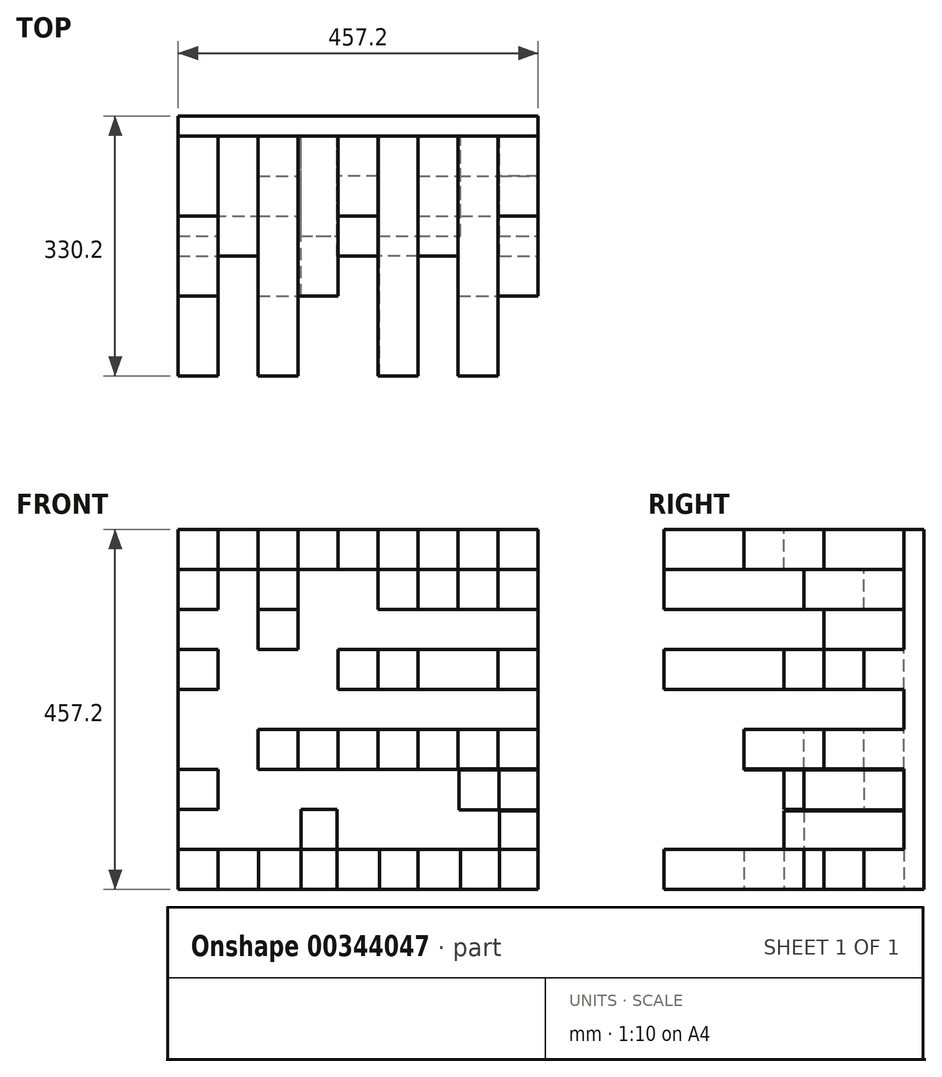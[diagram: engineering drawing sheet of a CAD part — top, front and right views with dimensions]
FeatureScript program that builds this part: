
annotation { "Feature Type Name" : "Feature", "Feature Type Description" : "" }
export const myFeature = defineFeature(function(context is Context, id is Id, definition is map)
    precondition{}
    {
        {
            var Q0;
            Q0=qCreatedBy(makeId("Front.planeOp"),FACE);
            var sketch = newSketch(context, id + "F0", { "sketchPlane" : qUnion([Q0])});
            skLineSegment(sketch, "E0.bottom", {"start": v(-230.78, 329.48) * mm, "end": v(226.42, 329.48) * mm});
            skLineSegment(sketch, "E0.top", {"start": v(-230.78, -127.72) * mm, "end": v(226.42, -127.72) * mm});
            skLineSegment(sketch, "E0.left", {"start": v(-230.78, 329.48) * mm, "end": v(-230.78, -127.72) * mm});
            skLineSegment(sketch, "E0.right", {"start": v(226.42, 329.48) * mm, "end": v(226.42, -127.72) * mm});
            skSolve(sketch);
        }
        {
            var Q0;
            Q0=makeQuery(id+"F0.imprint","IMPRINT",FACE,{"disambiguationData":[TD([[makeQuery(id+"F0.imprint","IMPRINT",EDGE,{"derivedFrom":sQuery(id+"F0.wireOp",EDGE,"E0.bottom")}),-1.0]])]});
            extrude(context, id + "F1", {"entities" : qUnion([Q0]), "depth" : 25.4 * mm});
        }
        {
            var Q0;
            Q0=makeQuery(id+"F1.opExtrude","CAP_FACE",FACE,{"disambiguationData":[OSD([sQuery(id+"F0.wireOp",EDGE,"E0.bottom"),sQuery(id+"F0.wireOp",EDGE,"E0.top"),sQuery(id+"F0.wireOp",EDGE,"E0.left"),sQuery(id+"F0.wireOp",EDGE,"E0.right")])],"isStart":false});
            var sketch = newSketch(context, id + "F2", { "sketchPlane" : qUnion([Q0])});
            skLineSegment(sketch, "E1.bottom", {"start": v(-230.78, 329.48) * mm, "end": v(-179.98, 329.48) * mm});
            skLineSegment(sketch, "E1.top", {"start": v(-230.78, 278.68) * mm, "end": v(-179.98, 278.68) * mm});
            skLineSegment(sketch, "E1.left", {"start": v(-230.78, 329.48) * mm, "end": v(-230.78, 278.68) * mm});
            skLineSegment(sketch, "E1.right", {"start": v(-179.98, 329.48) * mm, "end": v(-179.98, 278.68) * mm});
            skLineSegment(sketch, "E2.bottom", {"start": v(-179.98, 278.68) * mm, "end": v(-129.18, 278.68) * mm});
            skLineSegment(sketch, "E2.top", {"start": v(-179.98, 329.48) * mm, "end": v(-129.18, 329.48) * mm});
            skLineSegment(sketch, "E2.left", {"start": v(-179.98, 278.68) * mm, "end": v(-179.98, 329.48) * mm});
            skLineSegment(sketch, "E2.right", {"start": v(-129.18, 278.68) * mm, "end": v(-129.18, 329.48) * mm});
            skLineSegment(sketch, "E3.bottom", {"start": v(-129.18, 278.68) * mm, "end": v(-78.38, 278.68) * mm});
            skLineSegment(sketch, "E3.top", {"start": v(-129.18, 329.48) * mm, "end": v(-78.38, 329.48) * mm});
            skLineSegment(sketch, "E3.right", {"start": v(-78.38, 278.68) * mm, "end": v(-78.38, 329.48) * mm});
            skLineSegment(sketch, "E4.bottom", {"start": v(-78.38, 278.68) * mm, "end": v(-27.58, 278.68) * mm});
            skLineSegment(sketch, "E4.top", {"start": v(-78.38, 329.48) * mm, "end": v(-27.58, 329.48) * mm});
            skLineSegment(sketch, "E4.right", {"start": v(-27.58, 278.68) * mm, "end": v(-27.58, 329.48) * mm});
            skLineSegment(sketch, "E5.bottom", {"start": v(-27.58, 278.68) * mm, "end": v(23.22, 278.68) * mm});
            skLineSegment(sketch, "E5.top", {"start": v(-27.58, 329.48) * mm, "end": v(23.22, 329.48) * mm});
            skLineSegment(sketch, "E5.right", {"start": v(23.22, 278.68) * mm, "end": v(23.22, 329.48) * mm});
            skLineSegment(sketch, "E6.bottom", {"start": v(23.22, 278.68) * mm, "end": v(74.02, 278.68) * mm});
            skLineSegment(sketch, "E6.top", {"start": v(23.22, 329.48) * mm, "end": v(74.02, 329.48) * mm});
            skLineSegment(sketch, "E6.right", {"start": v(74.02, 278.68) * mm, "end": v(74.02, 329.48) * mm});
            skLineSegment(sketch, "E7.bottom", {"start": v(74.02, 278.68) * mm, "end": v(124.82, 278.68) * mm});
            skLineSegment(sketch, "E7.top", {"start": v(74.02, 329.48) * mm, "end": v(124.82, 329.48) * mm});
            skLineSegment(sketch, "E7.right", {"start": v(124.82, 278.68) * mm, "end": v(124.82, 329.48) * mm});
            skLineSegment(sketch, "E8.bottom", {"start": v(124.82, 278.68) * mm, "end": v(175.62, 278.68) * mm});
            skLineSegment(sketch, "E8.top", {"start": v(124.82, 329.48) * mm, "end": v(175.62, 329.48) * mm});
            skLineSegment(sketch, "E8.right", {"start": v(175.62, 278.68) * mm, "end": v(175.62, 329.48) * mm});
            skLineSegment(sketch, "E9.bottom", {"start": v(175.62, 278.68) * mm, "end": v(226.42, 278.68) * mm});
            skLineSegment(sketch, "E9.top", {"start": v(175.62, 329.48) * mm, "end": v(226.42, 329.48) * mm});
            skLineSegment(sketch, "E9.right", {"start": v(226.42, 278.68) * mm, "end": v(226.42, 329.48) * mm});
            skLineSegment(sketch, "E10.top", {"start": v(-230.78, 227.88) * mm, "end": v(-179.98, 227.88) * mm});
            skLineSegment(sketch, "E10.left", {"start": v(-230.78, 278.68) * mm, "end": v(-230.78, 227.88) * mm});
            skLineSegment(sketch, "E10.right", {"start": v(-179.98, 278.68) * mm, "end": v(-179.98, 227.88) * mm});
            skLineSegment(sketch, "E11.bottom", {"start": v(-179.98, 227.88) * mm, "end": v(-129.18, 227.88) * mm});
            skLineSegment(sketch, "E11.top", {"start": v(-179.98, 177.08) * mm, "end": v(-129.18, 177.08) * mm});
            skLineSegment(sketch, "E11.left", {"start": v(-179.98, 227.88) * mm, "end": v(-179.98, 177.08) * mm});
            skLineSegment(sketch, "E11.right", {"start": v(-129.18, 227.88) * mm, "end": v(-129.18, 177.08) * mm});
            skLineSegment(sketch, "E12.bottom", {"start": v(-129.18, 227.88) * mm, "end": v(-179.98, 227.88) * mm});
            skLineSegment(sketch, "E12.top", {"start": v(-129.18, 278.68) * mm, "end": v(-179.98, 278.68) * mm});
            skLineSegment(sketch, "E12.left", {"start": v(-129.18, 227.88) * mm, "end": v(-129.18, 278.68) * mm});
            skLineSegment(sketch, "E12.right", {"start": v(-179.98, 227.88) * mm, "end": v(-179.98, 278.68) * mm});
            skLineSegment(sketch, "E13.bottom", {"start": v(-129.18, 227.88) * mm, "end": v(-78.38, 227.88) * mm});
            skLineSegment(sketch, "E13.right", {"start": v(-78.38, 227.88) * mm, "end": v(-78.38, 278.68) * mm});
            skLineSegment(sketch, "E14.bottom", {"start": v(-78.38, 227.88) * mm, "end": v(-27.58, 227.88) * mm});
            skLineSegment(sketch, "E14.right", {"start": v(-27.58, 227.88) * mm, "end": v(-27.58, 278.68) * mm});
            skLineSegment(sketch, "E15.bottom", {"start": v(-27.58, 227.88) * mm, "end": v(23.22, 227.88) * mm});
            skLineSegment(sketch, "E15.right", {"start": v(23.22, 227.88) * mm, "end": v(23.22, 278.68) * mm});
            skLineSegment(sketch, "E16.bottom", {"start": v(23.22, 227.88) * mm, "end": v(74.02, 227.88) * mm});
            skLineSegment(sketch, "E16.right", {"start": v(74.02, 227.88) * mm, "end": v(74.02, 278.68) * mm});
            skLineSegment(sketch, "E17.bottom", {"start": v(74.02, 227.88) * mm, "end": v(124.82, 227.88) * mm});
            skLineSegment(sketch, "E17.right", {"start": v(124.82, 227.88) * mm, "end": v(124.82, 278.68) * mm});
            skLineSegment(sketch, "E18.bottom", {"start": v(124.82, 227.88) * mm, "end": v(175.62, 227.88) * mm});
            skLineSegment(sketch, "E18.right", {"start": v(175.62, 227.88) * mm, "end": v(175.62, 278.68) * mm});
            skLineSegment(sketch, "E19.bottom", {"start": v(175.62, 227.88) * mm, "end": v(226.42, 227.88) * mm});
            skLineSegment(sketch, "E19.right", {"start": v(226.42, 227.88) * mm, "end": v(226.42, 278.68) * mm});
            skLineSegment(sketch, "E20.bottom", {"start": v(-179.98, 227.88) * mm, "end": v(-230.78, 227.88) * mm});
            skLineSegment(sketch, "E20.top", {"start": v(-179.98, 177.08) * mm, "end": v(-230.78, 177.08) * mm});
            skLineSegment(sketch, "E20.right", {"start": v(-230.78, 227.88) * mm, "end": v(-230.78, 177.08) * mm});
            skLineSegment(sketch, "E21.bottom", {"start": v(-129.18, 177.08) * mm, "end": v(-78.38, 177.08) * mm});
            skLineSegment(sketch, "E21.left", {"start": v(-129.18, 177.08) * mm, "end": v(-129.18, 227.88) * mm});
            skLineSegment(sketch, "E21.right", {"start": v(-78.38, 177.08) * mm, "end": v(-78.38, 227.88) * mm});
            skLineSegment(sketch, "E22.bottom", {"start": v(-27.58, 227.88) * mm, "end": v(-78.38, 227.88) * mm});
            skLineSegment(sketch, "E22.top", {"start": v(-27.58, 177.08) * mm, "end": v(-78.38, 177.08) * mm});
            skLineSegment(sketch, "E22.left", {"start": v(-27.58, 227.88) * mm, "end": v(-27.58, 177.08) * mm});
            skLineSegment(sketch, "E22.right", {"start": v(-78.38, 227.88) * mm, "end": v(-78.38, 177.08) * mm});
            skLineSegment(sketch, "E23.bottom", {"start": v(23.22, 227.88) * mm, "end": v(-27.58, 227.88) * mm});
            skLineSegment(sketch, "E23.top", {"start": v(23.22, 177.08) * mm, "end": v(-27.58, 177.08) * mm});
            skLineSegment(sketch, "E23.left", {"start": v(23.22, 227.88) * mm, "end": v(23.22, 177.08) * mm});
            skLineSegment(sketch, "E24.bottom", {"start": v(74.02, 227.88) * mm, "end": v(23.22, 227.88) * mm});
            skLineSegment(sketch, "E24.top", {"start": v(74.02, 177.08) * mm, "end": v(23.22, 177.08) * mm});
            skLineSegment(sketch, "E24.left", {"start": v(74.02, 227.88) * mm, "end": v(74.02, 177.08) * mm});
            skLineSegment(sketch, "E25.bottom", {"start": v(124.82, 227.88) * mm, "end": v(74.02, 227.88) * mm});
            skLineSegment(sketch, "E25.top", {"start": v(124.82, 177.08) * mm, "end": v(74.02, 177.08) * mm});
            skLineSegment(sketch, "E25.left", {"start": v(124.82, 227.88) * mm, "end": v(124.82, 177.08) * mm});
            skLineSegment(sketch, "E26.bottom", {"start": v(175.62, 227.88) * mm, "end": v(124.82, 227.88) * mm});
            skLineSegment(sketch, "E26.top", {"start": v(175.62, 177.08) * mm, "end": v(124.82, 177.08) * mm});
            skLineSegment(sketch, "E26.left", {"start": v(175.62, 227.88) * mm, "end": v(175.62, 177.08) * mm});
            skLineSegment(sketch, "E27.bottom", {"start": v(226.42, 227.88) * mm, "end": v(175.62, 227.88) * mm});
            skLineSegment(sketch, "E27.top", {"start": v(226.42, 177.08) * mm, "end": v(175.62, 177.08) * mm});
            skLineSegment(sketch, "E27.left", {"start": v(226.42, 227.88) * mm, "end": v(226.42, 177.08) * mm});
            skLineSegment(sketch, "E28.top", {"start": v(226.42, 126.28) * mm, "end": v(175.62, 126.28) * mm});
            skLineSegment(sketch, "E28.left", {"start": v(226.42, 177.08) * mm, "end": v(226.42, 126.28) * mm});
            skLineSegment(sketch, "E28.right", {"start": v(175.62, 177.08) * mm, "end": v(175.62, 126.28) * mm});
            skLineSegment(sketch, "E29.bottom", {"start": v(175.62, 126.28) * mm, "end": v(124.82, 126.28) * mm});
            skLineSegment(sketch, "E29.left", {"start": v(175.62, 126.28) * mm, "end": v(175.62, 177.08) * mm});
            skLineSegment(sketch, "E29.right", {"start": v(124.82, 126.28) * mm, "end": v(124.82, 177.08) * mm});
            skLineSegment(sketch, "E30.bottom", {"start": v(124.82, 126.28) * mm, "end": v(74.02, 126.28) * mm});
            skLineSegment(sketch, "E30.right", {"start": v(74.02, 126.28) * mm, "end": v(74.02, 177.08) * mm});
            skLineSegment(sketch, "E31.bottom", {"start": v(74.02, 126.28) * mm, "end": v(23.22, 126.28) * mm});
            skLineSegment(sketch, "E31.right", {"start": v(23.22, 126.28) * mm, "end": v(23.22, 177.08) * mm});
            skLineSegment(sketch, "E32.bottom", {"start": v(23.22, 126.28) * mm, "end": v(-27.58, 126.28) * mm});
            skLineSegment(sketch, "E32.right", {"start": v(-27.58, 126.28) * mm, "end": v(-27.58, 177.08) * mm});
            skLineSegment(sketch, "E33.bottom", {"start": v(-27.58, 126.28) * mm, "end": v(-78.38, 126.28) * mm});
            skLineSegment(sketch, "E33.right", {"start": v(-78.38, 126.28) * mm, "end": v(-78.38, 177.08) * mm});
            skLineSegment(sketch, "E34.bottom", {"start": v(-78.38, 126.28) * mm, "end": v(-129.18, 126.28) * mm});
            skLineSegment(sketch, "E34.top", {"start": v(-78.38, 177.08) * mm, "end": v(-129.18, 177.08) * mm});
            skLineSegment(sketch, "E34.right", {"start": v(-129.18, 126.28) * mm, "end": v(-129.18, 177.08) * mm});
            skLineSegment(sketch, "E35.bottom", {"start": v(-129.18, 126.28) * mm, "end": v(-179.98, 126.28) * mm});
            skLineSegment(sketch, "E35.top", {"start": v(-129.18, 177.08) * mm, "end": v(-179.98, 177.08) * mm});
            skLineSegment(sketch, "E35.right", {"start": v(-179.98, 126.28) * mm, "end": v(-179.98, 177.08) * mm});
            skLineSegment(sketch, "E36.bottom", {"start": v(-179.98, 126.28) * mm, "end": v(-230.78, 126.28) * mm});
            skLineSegment(sketch, "E36.right", {"start": v(-230.78, 126.28) * mm, "end": v(-230.78, 177.08) * mm});
            skLineSegment(sketch, "E37.bottom", {"start": v(-230.78, 126.28) * mm, "end": v(-179.98, 126.28) * mm});
            skLineSegment(sketch, "E37.top", {"start": v(-230.78, 75.48) * mm, "end": v(-179.98, 75.48) * mm});
            skLineSegment(sketch, "E37.left", {"start": v(-230.78, 126.28) * mm, "end": v(-230.78, 75.48) * mm});
            skLineSegment(sketch, "E37.right", {"start": v(-179.98, 126.28) * mm, "end": v(-179.98, 75.48) * mm});
            skLineSegment(sketch, "E38.bottom", {"start": v(-179.98, 75.48) * mm, "end": v(-129.18, 75.48) * mm});
            skLineSegment(sketch, "E38.top", {"start": v(-179.98, 126.28) * mm, "end": v(-129.18, 126.28) * mm});
            skLineSegment(sketch, "E38.left", {"start": v(-179.98, 75.48) * mm, "end": v(-179.98, 126.28) * mm});
            skLineSegment(sketch, "E38.right", {"start": v(-129.18, 75.48) * mm, "end": v(-129.18, 126.28) * mm});
            skLineSegment(sketch, "E39.bottom", {"start": v(-129.18, 75.48) * mm, "end": v(-78.38, 75.48) * mm});
            skLineSegment(sketch, "E39.top", {"start": v(-129.18, 126.28) * mm, "end": v(-78.38, 126.28) * mm});
            skLineSegment(sketch, "E39.right", {"start": v(-78.38, 75.48) * mm, "end": v(-78.38, 126.28) * mm});
            skLineSegment(sketch, "E40.bottom", {"start": v(-78.38, 75.48) * mm, "end": v(-27.58, 75.48) * mm});
            skLineSegment(sketch, "E40.top", {"start": v(-78.38, 126.28) * mm, "end": v(-27.58, 126.28) * mm});
            skLineSegment(sketch, "E40.right", {"start": v(-27.58, 75.48) * mm, "end": v(-27.58, 126.28) * mm});
            skLineSegment(sketch, "E41.bottom", {"start": v(-27.58, 75.48) * mm, "end": v(23.22, 75.48) * mm});
            skLineSegment(sketch, "E41.top", {"start": v(-27.58, 126.28) * mm, "end": v(23.22, 126.28) * mm});
            skLineSegment(sketch, "E41.right", {"start": v(23.22, 75.48) * mm, "end": v(23.22, 126.28) * mm});
            skLineSegment(sketch, "E42.bottom", {"start": v(23.22, 75.48) * mm, "end": v(74.02, 75.48) * mm});
            skLineSegment(sketch, "E42.top", {"start": v(23.22, 126.28) * mm, "end": v(74.02, 126.28) * mm});
            skLineSegment(sketch, "E42.right", {"start": v(74.02, 75.48) * mm, "end": v(74.02, 126.28) * mm});
            skLineSegment(sketch, "E43.bottom", {"start": v(74.02, 75.48) * mm, "end": v(124.82, 75.48) * mm});
            skLineSegment(sketch, "E43.top", {"start": v(74.02, 126.28) * mm, "end": v(124.82, 126.28) * mm});
            skLineSegment(sketch, "E43.right", {"start": v(124.82, 75.48) * mm, "end": v(124.82, 126.28) * mm});
            skLineSegment(sketch, "E44.bottom", {"start": v(124.82, 75.48) * mm, "end": v(175.62, 75.48) * mm});
            skLineSegment(sketch, "E44.top", {"start": v(124.82, 126.28) * mm, "end": v(175.62, 126.28) * mm});
            skLineSegment(sketch, "E44.right", {"start": v(175.62, 75.48) * mm, "end": v(175.62, 126.28) * mm});
            skLineSegment(sketch, "E45.bottom", {"start": v(175.62, 75.48) * mm, "end": v(226.42, 75.48) * mm});
            skLineSegment(sketch, "E45.top", {"start": v(175.62, 126.28) * mm, "end": v(226.42, 126.28) * mm});
            skLineSegment(sketch, "E45.right", {"start": v(226.42, 75.48) * mm, "end": v(226.42, 126.28) * mm});
            skLineSegment(sketch, "E46.top", {"start": v(-230.78, 24.68) * mm, "end": v(-179.98, 24.68) * mm});
            skLineSegment(sketch, "E46.left", {"start": v(-230.78, 75.48) * mm, "end": v(-230.78, 24.68) * mm});
            skLineSegment(sketch, "E46.right", {"start": v(-179.98, 75.48) * mm, "end": v(-179.98, 24.68) * mm});
            skLineSegment(sketch, "E47.bottom", {"start": v(-179.98, 24.68) * mm, "end": v(-129.18, 24.68) * mm});
            skLineSegment(sketch, "E47.left", {"start": v(-179.98, 24.68) * mm, "end": v(-179.98, 75.48) * mm});
            skLineSegment(sketch, "E47.right", {"start": v(-129.18, 24.68) * mm, "end": v(-129.18, 75.48) * mm});
            skLineSegment(sketch, "E48.bottom", {"start": v(-129.18, 24.68) * mm, "end": v(-78.38, 24.68) * mm});
            skLineSegment(sketch, "E48.right", {"start": v(-78.38, 24.68) * mm, "end": v(-78.38, 75.48) * mm});
            skLineSegment(sketch, "E49.bottom", {"start": v(-78.38, 24.68) * mm, "end": v(-27.58, 24.68) * mm});
            skLineSegment(sketch, "E49.right", {"start": v(-27.58, 24.68) * mm, "end": v(-27.58, 75.48) * mm});
            skLineSegment(sketch, "E50.bottom", {"start": v(-27.58, 24.68) * mm, "end": v(23.22, 24.68) * mm});
            skLineSegment(sketch, "E50.right", {"start": v(23.22, 24.68) * mm, "end": v(23.22, 75.48) * mm});
            skLineSegment(sketch, "E51.bottom", {"start": v(23.22, 24.68) * mm, "end": v(74.02, 24.68) * mm});
            skLineSegment(sketch, "E51.right", {"start": v(74.02, 24.68) * mm, "end": v(74.02, 75.48) * mm});
            skLineSegment(sketch, "E52.bottom", {"start": v(74.02, 24.68) * mm, "end": v(124.82, 24.68) * mm});
            skLineSegment(sketch, "E52.right", {"start": v(124.82, 24.68) * mm, "end": v(124.82, 75.48) * mm});
            skLineSegment(sketch, "E53.bottom", {"start": v(124.1, 24.03) * mm, "end": v(175.62, 24.03) * mm});
            skLineSegment(sketch, "E53.top", {"start": v(124.1, 75.48) * mm, "end": v(175.62, 75.48) * mm});
            skLineSegment(sketch, "E53.left", {"start": v(124.1, 24.03) * mm, "end": v(124.1, 75.48) * mm});
            skLineSegment(sketch, "E53.right", {"start": v(175.62, 24.03) * mm, "end": v(175.62, 75.48) * mm});
            skLineSegment(sketch, "E54.bottom", {"start": v(175.62, 24.03) * mm, "end": v(226.42, 24.03) * mm});
            skLineSegment(sketch, "E54.right", {"start": v(226.42, 24.03) * mm, "end": v(226.42, 75.48) * mm});
            skLineSegment(sketch, "E55.top", {"start": v(-230.78, -26.12) * mm, "end": v(-179.98, -26.12) * mm});
            skLineSegment(sketch, "E55.left", {"start": v(-230.78, 24.68) * mm, "end": v(-230.78, -26.12) * mm});
            skLineSegment(sketch, "E55.right", {"start": v(-179.98, 24.68) * mm, "end": v(-179.98, -26.12) * mm});
            skLineSegment(sketch, "E56.top", {"start": v(-179.98, -26.12) * mm, "end": v(-129.18, -26.12) * mm});
            skLineSegment(sketch, "E56.right", {"start": v(-129.18, 24.68) * mm, "end": v(-129.18, -26.12) * mm});
            skLineSegment(sketch, "E57.top", {"start": v(-129.18, -26.12) * mm, "end": v(-78.38, -26.12) * mm});
            skLineSegment(sketch, "E57.right", {"start": v(-78.38, 24.68) * mm, "end": v(-78.38, -26.12) * mm});
            skLineSegment(sketch, "E58.top", {"start": v(-78.38, -26.32) * mm, "end": v(-27.58, -26.32) * mm});
            skLineSegment(sketch, "E58.left", {"start": v(-78.38, 24.68) * mm, "end": v(-78.38, -26.32) * mm});
            skLineSegment(sketch, "E58.right", {"start": v(-27.58, 24.68) * mm, "end": v(-27.58, -26.32) * mm});
            skLineSegment(sketch, "E59.bottom", {"start": v(-27.58, 24.68) * mm, "end": v(22, 24.68) * mm});
            skLineSegment(sketch, "E59.top", {"start": v(-27.58, -26.27) * mm, "end": v(22, -26.27) * mm});
            skLineSegment(sketch, "E59.left", {"start": v(-27.58, 24.68) * mm, "end": v(-27.58, -26.27) * mm});
            skLineSegment(sketch, "E59.right", {"start": v(22, 24.68) * mm, "end": v(22, -26.27) * mm});
            skLineSegment(sketch, "E60.bottom", {"start": v(23.22, 24.68) * mm, "end": v(73.8, 24.68) * mm});
            skLineSegment(sketch, "E60.top", {"start": v(23.22, -26.97) * mm, "end": v(73.8, -26.97) * mm});
            skLineSegment(sketch, "E60.left", {"start": v(23.22, 24.68) * mm, "end": v(23.22, -26.97) * mm});
            skLineSegment(sketch, "E60.right", {"start": v(73.8, 24.68) * mm, "end": v(73.8, -26.97) * mm});
            skLineSegment(sketch, "E61.bottom", {"start": v(74.02, 24.68) * mm, "end": v(124.85, 24.68) * mm});
            skLineSegment(sketch, "E61.top", {"start": v(74.02, -27.67) * mm, "end": v(124.85, -27.67) * mm});
            skLineSegment(sketch, "E61.left", {"start": v(74.02, 24.68) * mm, "end": v(74.02, -27.67) * mm});
            skLineSegment(sketch, "E61.right", {"start": v(124.85, 24.68) * mm, "end": v(124.85, -27.67) * mm});
            skLineSegment(sketch, "E62.bottom", {"start": v(125.6, 25.53) * mm, "end": v(176.64, 25.53) * mm});
            skLineSegment(sketch, "E62.top", {"start": v(125.6, -26.87) * mm, "end": v(176.64, -26.87) * mm});
            skLineSegment(sketch, "E62.left", {"start": v(125.6, 25.53) * mm, "end": v(125.6, -26.87) * mm});
            skLineSegment(sketch, "E62.right", {"start": v(176.64, 25.53) * mm, "end": v(176.64, -26.87) * mm});
            skLineSegment(sketch, "E63.bottom", {"start": v(176.64, 25.53) * mm, "end": v(226.42, 25.53) * mm});
            skLineSegment(sketch, "E63.top", {"start": v(176.64, -26.82) * mm, "end": v(226.42, -26.82) * mm});
            skLineSegment(sketch, "E63.left", {"start": v(176.64, 25.53) * mm, "end": v(176.64, -26.82) * mm});
            skLineSegment(sketch, "E63.right", {"start": v(226.42, 25.53) * mm, "end": v(226.42, -26.82) * mm});
            skLineSegment(sketch, "E64.bottom", {"start": v(-230.78, -127.72) * mm, "end": v(-179.98, -127.72) * mm});
            skLineSegment(sketch, "E64.top", {"start": v(-230.78, -76.92) * mm, "end": v(-179.98, -76.92) * mm});
            skLineSegment(sketch, "E64.left", {"start": v(-230.78, -127.72) * mm, "end": v(-230.78, -76.92) * mm});
            skLineSegment(sketch, "E64.right", {"start": v(-179.98, -127.72) * mm, "end": v(-179.98, -76.92) * mm});
            skLineSegment(sketch, "E65.bottom", {"start": v(-179.98, -76.92) * mm, "end": v(-128.89, -76.92) * mm});
            skLineSegment(sketch, "E65.top", {"start": v(-179.98, -127.72) * mm, "end": v(-128.89, -127.72) * mm});
            skLineSegment(sketch, "E65.left", {"start": v(-179.98, -76.92) * mm, "end": v(-179.98, -127.72) * mm});
            skLineSegment(sketch, "E65.right", {"start": v(-128.89, -76.92) * mm, "end": v(-128.89, -127.72) * mm});
            skLineSegment(sketch, "E66.bottom", {"start": v(-128.89, -76.92) * mm, "end": v(-74.84, -76.92) * mm});
            skLineSegment(sketch, "E66.top", {"start": v(-128.89, -127.72) * mm, "end": v(-74.84, -127.72) * mm});
            skLineSegment(sketch, "E66.right", {"start": v(-74.84, -76.92) * mm, "end": v(-74.84, -127.72) * mm});
            skLineSegment(sketch, "E67.bottom", {"start": v(-74.84, -76.92) * mm, "end": v(-29.05, -76.92) * mm});
            skLineSegment(sketch, "E67.top", {"start": v(-74.84, -127.72) * mm, "end": v(-29.05, -127.72) * mm});
            skLineSegment(sketch, "E67.right", {"start": v(-29.05, -76.92) * mm, "end": v(-29.05, -127.72) * mm});
            skLineSegment(sketch, "E68.bottom", {"start": v(-29.05, -76.92) * mm, "end": v(25, -76.92) * mm});
            skLineSegment(sketch, "E68.top", {"start": v(-29.05, -127.72) * mm, "end": v(25, -127.72) * mm});
            skLineSegment(sketch, "E68.right", {"start": v(25, -76.92) * mm, "end": v(25, -127.72) * mm});
            skLineSegment(sketch, "E69.bottom", {"start": v(25, -76.92) * mm, "end": v(73.79, -76.92) * mm});
            skLineSegment(sketch, "E69.top", {"start": v(25, -127.72) * mm, "end": v(73.79, -127.72) * mm});
            skLineSegment(sketch, "E69.right", {"start": v(73.79, -76.92) * mm, "end": v(73.79, -127.72) * mm});
            skLineSegment(sketch, "E70.bottom", {"start": v(73.79, -76.92) * mm, "end": v(127.83, -76.92) * mm});
            skLineSegment(sketch, "E70.top", {"start": v(73.79, -127.72) * mm, "end": v(127.83, -127.72) * mm});
            skLineSegment(sketch, "E70.right", {"start": v(127.83, -76.92) * mm, "end": v(127.83, -127.72) * mm});
            skLineSegment(sketch, "E71.bottom", {"start": v(127.83, -76.92) * mm, "end": v(177.38, -76.92) * mm});
            skLineSegment(sketch, "E71.top", {"start": v(127.83, -127.72) * mm, "end": v(177.38, -127.72) * mm});
            skLineSegment(sketch, "E71.right", {"start": v(177.38, -76.92) * mm, "end": v(177.38, -127.72) * mm});
            skLineSegment(sketch, "E72.bottom", {"start": v(177.38, -76.92) * mm, "end": v(226.42, -76.92) * mm});
            skLineSegment(sketch, "E72.top", {"start": v(177.38, -127.72) * mm, "end": v(226.42, -127.72) * mm});
            skLineSegment(sketch, "E72.right", {"start": v(226.42, -76.92) * mm, "end": v(226.42, -127.72) * mm});
            skLineSegment(sketch, "E73.left", {"start": v(-230.78, -26.12) * mm, "end": v(-230.78, -76.92) * mm});
            skLineSegment(sketch, "E73.right", {"start": v(-179.98, -26.12) * mm, "end": v(-179.98, -76.92) * mm});
            skLineSegment(sketch, "E74.bottom", {"start": v(-179.98, -26.12) * mm, "end": v(-128.89, -26.12) * mm});
            skLineSegment(sketch, "E74.right", {"start": v(-128.89, -26.12) * mm, "end": v(-128.89, -76.92) * mm});
            skLineSegment(sketch, "E75.bottom", {"start": v(-128.89, -26.12) * mm, "end": v(-74.84, -26.12) * mm});
            skLineSegment(sketch, "E75.right", {"start": v(-74.84, -26.12) * mm, "end": v(-74.84, -76.92) * mm});
            skLineSegment(sketch, "E76.bottom", {"start": v(-74.84, -26.12) * mm, "end": v(-29.05, -26.12) * mm});
            skLineSegment(sketch, "E76.right", {"start": v(-29.05, -26.12) * mm, "end": v(-29.05, -76.92) * mm});
            skLineSegment(sketch, "E77.bottom", {"start": v(-27.58, -26.27) * mm, "end": v(25, -26.27) * mm});
            skLineSegment(sketch, "E77.top", {"start": v(-27.58, -76.92) * mm, "end": v(25, -76.92) * mm});
            skLineSegment(sketch, "E77.left", {"start": v(-27.58, -26.27) * mm, "end": v(-27.58, -76.92) * mm});
            skLineSegment(sketch, "E77.right", {"start": v(25, -26.27) * mm, "end": v(25, -76.92) * mm});
            skLineSegment(sketch, "E78.bottom", {"start": v(25, -26.27) * mm, "end": v(73.79, -26.27) * mm});
            skLineSegment(sketch, "E78.right", {"start": v(73.79, -26.27) * mm, "end": v(73.79, -76.92) * mm});
            skLineSegment(sketch, "E79.bottom", {"start": v(74.02, -27.67) * mm, "end": v(127.83, -27.67) * mm});
            skLineSegment(sketch, "E79.top", {"start": v(74.02, -76.92) * mm, "end": v(127.83, -76.92) * mm});
            skLineSegment(sketch, "E79.left", {"start": v(74.02, -27.67) * mm, "end": v(74.02, -76.92) * mm});
            skLineSegment(sketch, "E79.right", {"start": v(127.83, -27.67) * mm, "end": v(127.83, -76.92) * mm});
            skLineSegment(sketch, "E80.bottom", {"start": v(127.83, -27.67) * mm, "end": v(177.38, -27.67) * mm});
            skLineSegment(sketch, "E80.right", {"start": v(177.38, -27.67) * mm, "end": v(177.38, -76.92) * mm});
            skLineSegment(sketch, "E81.bottom", {"start": v(177.38, -27.67) * mm, "end": v(226.42, -27.67) * mm});
            skLineSegment(sketch, "E81.right", {"start": v(226.42, -27.67) * mm, "end": v(226.42, -76.92) * mm});
            skSolve(sketch);
        }
        {
            var Q0;
            Q0=makeQuery(id+"F2.imprint","IMPRINT",FACE,{"disambiguationData":[TD([[makeQuery(id+"F2.imprint","IMPRINT",EDGE,{"derivedFrom":sQuery(id+"F2.wireOp",EDGE,"E3.bottom")}),-1.0]])]});
            var Q1;
            Q1=makeQuery(id+"F2.imprint","IMPRINT",FACE,{"disambiguationData":[TD([[makeQuery(id+"F2.imprint","IMPRINT",EDGE,{"derivedFrom":sQuery(id+"F2.wireOp",EDGE,"E72.top")}),1.0]])]});
            var Q2;
            Q2=makeQuery(id+"F2.imprint","IMPRINT",FACE,{"disambiguationData":[TD([[makeQuery(id+"F2.imprint","IMPRINT",EDGE,{"derivedFrom":sQuery(id+"F2.wireOp",EDGE,"E50.bottom")}),1.0]])]});
            var Q3;
            Q3=makeQuery(id+"F2.imprint","IMPRINT",FACE,{"disambiguationData":[TD([[makeQuery(id+"F2.imprint","IMPRINT",EDGE,{"derivedFrom":sQuery(id+"F2.wireOp",EDGE,"E65.bottom")}),1.0]])]});
            var Q4;
            Q4=makeQuery(id+"F2.imprint","IMPRINT",FACE,{"disambiguationData":[TD([[makeQuery(id+"F2.imprint","IMPRINT",EDGE,{"derivedFrom":sQuery(id+"F2.wireOp",EDGE,"E7.bottom")}),-1.0]])]});
            var Q5;
            Q5=makeQuery(id+"F2.imprint","IMPRINT",FACE,{"disambiguationData":[TD([[makeQuery(id+"F2.imprint","IMPRINT",EDGE,{"derivedFrom":sQuery(id+"F2.wireOp",EDGE,"E38.bottom")}),-1.0]])]});
            var Q6;
            Q6=makeQuery(id+"F2.imprint","IMPRINT",FACE,{"disambiguationData":[TD([[makeQuery(id+"F2.imprint","IMPRINT",EDGE,{"derivedFrom":sQuery(id+"F2.wireOp",EDGE,"E27.top")}),1.0]])]});
            var Q7;
            Q7=makeQuery(id+"F2.imprint","IMPRINT",FACE,{"disambiguationData":[TD([[makeQuery(id+"F2.imprint","IMPRINT",EDGE,{"derivedFrom":sQuery(id+"F2.wireOp",EDGE,"E23.top")}),1.0]])]});
            var Q8;
            {var subQ1=sQuery(id+"F2.wireOp",EDGE,"E62.top");Q8=makeQuery(id+"F2.imprint","IMPRINT",FACE,{"disambiguationData":[TD([[makeQuery(id+"F2.imprint","IMPRINT",EDGE,{"derivedFrom":subQ1}),1.0]])]});}
            extrude(context, id + "F3", {"entities" : qUnion([Q0, Q1, Q2, Q3, Q4, Q5, Q6, Q7, Q8]), "operationType" : NewBodyOperationType.ADD, "depth" : 50.8 * mm});
        }
        {
            var Q0;
            Q0=makeQuery(id+"F2.imprint","IMPRINT",FACE,{"disambiguationData":[TD([[makeQuery(id+"F2.imprint","IMPRINT",EDGE,{"derivedFrom":sQuery(id+"F2.wireOp",EDGE,"E1.bottom")}),-1.0]])]});
            var Q1;
            Q1=makeQuery(id+"F2.imprint","IMPRINT",FACE,{"disambiguationData":[TD([[makeQuery(id+"F2.imprint","IMPRINT",EDGE,{"derivedFrom":sQuery(id+"F2.wireOp",EDGE,"E5.top")}),-1.0]])]});
            var Q2;
            Q2=makeQuery(id+"F2.imprint","IMPRINT",FACE,{"disambiguationData":[TD([[makeQuery(id+"F2.imprint","IMPRINT",EDGE,{"derivedFrom":sQuery(id+"F2.wireOp",EDGE,"E34.top")}),1.0]])]});
            var Q3;
            {var subQ0=sQuery(id+"F2.wireOp",EDGE,"E43.bottom");Q3=makeQuery(id+"F2.imprint","IMPRINT",FACE,{"disambiguationData":[TD([[makeQuery(id+"F2.imprint","IMPRINT",EDGE,{"derivedFrom":subQ0}),-1.0]])]});}
            var Q4;
            Q4=makeQuery(id+"F2.imprint","IMPRINT",FACE,{"disambiguationData":[TD([[makeQuery(id+"F2.imprint","IMPRINT",EDGE,{"derivedFrom":sQuery(id+"F2.wireOp",EDGE,"E68.bottom")}),-1.0]])]});
            var Q5;
            Q5=makeQuery(id+"F2.imprint","IMPRINT",FACE,{"disambiguationData":[TD([[makeQuery(id+"F2.imprint","IMPRINT",EDGE,{"derivedFrom":sQuery(id+"F2.wireOp",EDGE,"E9.top")}),-1.0]])]});
            var Q6;
            Q6=makeQuery(id+"F2.imprint","IMPRINT",FACE,{"disambiguationData":[TD([[makeQuery(id+"F2.imprint","IMPRINT",EDGE,{"derivedFrom":sQuery(id+"F2.wireOp",EDGE,"E25.top")}),1.0]])]});
            var Q7;
            Q7=makeQuery(id+"F2.imprint","IMPRINT",FACE,{"disambiguationData":[TD([[makeQuery(id+"F2.imprint","IMPRINT",EDGE,{"derivedFrom":sQuery(id+"F2.wireOp",EDGE,"E20.bottom")}),1.0]])]});
            var Q8;
            Q8=makeQuery(id+"F2.imprint","IMPRINT",FACE,{"disambiguationData":[TD([[makeQuery(id+"F2.imprint","IMPRINT",EDGE,{"derivedFrom":sQuery(id+"F2.wireOp",EDGE,"E64.bottom")}),1.0]])]});
            var Q9;
            {var subQ5=sQuery(id+"F2.wireOp",EDGE,"E48.bottom");Q9=makeQuery(id+"F2.imprint","IMPRINT",FACE,{"disambiguationData":[TD([[makeQuery(id+"F2.imprint","IMPRINT",EDGE,{"derivedFrom":subQ5}),-1.0]])]});}
            var Q10;
            Q10=makeQuery(id+"F2.imprint","IMPRINT",FACE,{"disambiguationData":[TD([[makeQuery(id+"F2.imprint","IMPRINT",EDGE,{"derivedFrom":sQuery(id+"F2.wireOp",EDGE,"E37.bottom")}),-1.0]])]});
            var Q11;
            Q11=makeQuery(id+"F2.imprint","IMPRINT",FACE,{"disambiguationData":[TD([[makeQuery(id+"F2.imprint","IMPRINT",EDGE,{"derivedFrom":sQuery(id+"F2.wireOp",EDGE,"E22.bottom")}),1.0]])]});
            var Q12;
            Q12=makeQuery(id+"F2.imprint","IMPRINT",FACE,{"disambiguationData":[TD([[makeQuery(id+"F2.imprint","IMPRINT",EDGE,{"derivedFrom":sQuery(id+"F2.wireOp",EDGE,"E26.bottom")}),1.0]])]});
            var Q13;
            {var subQ4=sQuery(id+"F2.wireOp",EDGE,"E45.bottom");Q13=makeQuery(id+"F2.imprint","IMPRINT",FACE,{"disambiguationData":[TD([[makeQuery(id+"F2.imprint","IMPRINT",EDGE,{"derivedFrom":subQ4}),-1.0]])]});}
            var Q14;
            Q14=makeQuery(id+"F2.imprint","IMPRINT",FACE,{"disambiguationData":[TD([[makeQuery(id+"F2.imprint","IMPRINT",EDGE,{"derivedFrom":sQuery(id+"F2.wireOp",EDGE,"E71.top")}),1.0]])]});
            var Q15;
            Q15=makeQuery(id+"F2.imprint","IMPRINT",FACE,{"disambiguationData":[TD([[makeQuery(id+"F2.imprint","IMPRINT",EDGE,{"derivedFrom":sQuery(id+"F2.wireOp",EDGE,"E25.bottom")}),1.0]])]});
            var Q16;
            Q16=makeQuery(id+"F2.imprint","IMPRINT",FACE,{"disambiguationData":[TD([[makeQuery(id+"F2.imprint","IMPRINT",EDGE,{"derivedFrom":sQuery(id+"F2.wireOp",EDGE,"E26.top")}),1.0]])]});
            var Q17;
            Q17=makeQuery(id+"F2.imprint","IMPRINT",FACE,{"disambiguationData":[TD([[makeQuery(id+"F2.imprint","IMPRINT",EDGE,{"derivedFrom":sQuery(id+"F2.wireOp",EDGE,"E13.bottom")}),-1.0]])]});
            var Q18;
            Q18=makeQuery(id+"F2.imprint","IMPRINT",FACE,{"disambiguationData":[TD([[makeQuery(id+"F2.imprint","IMPRINT",EDGE,{"derivedFrom":sQuery(id+"F2.wireOp",EDGE,"E22.top")}),1.0]])]});
            var Q19;
            Q19=makeQuery(id+"F2.imprint","IMPRINT",FACE,{"disambiguationData":[TD([[makeQuery(id+"F2.imprint","IMPRINT",EDGE,{"derivedFrom":sQuery(id+"F2.wireOp",EDGE,"E37.top")}),-1.0]])]});
            var Q20;
            Q20=makeQuery(id+"F2.imprint","IMPRINT",FACE,{"disambiguationData":[TD([[makeQuery(id+"F2.imprint","IMPRINT",EDGE,{"derivedFrom":sQuery(id+"F2.wireOp",EDGE,"E39.bottom")}),-1.0]])]});
            var Q21;
            Q21=makeQuery(id+"F2.imprint","IMPRINT",FACE,{"disambiguationData":[TD([[makeQuery(id+"F2.imprint","IMPRINT",EDGE,{"derivedFrom":sQuery(id+"F2.wireOp",EDGE,"E65.top")}),1.0]])]});
            extrude(context, id + "F4", {"entities" : qUnion([Q0, Q1, Q2, Q3, Q4, Q5, Q6, Q7, Q8, Q9, Q10, Q11, Q12, Q13, Q14, Q15, Q16, Q17, Q18, Q19, Q20, Q21]), "operationType" : NewBodyOperationType.ADD, "depth" : 101.6 * mm});
        }
        {
            var Q0;
            Q0=makeQuery(id+"F2.imprint","IMPRINT",FACE,{"disambiguationData":[TD([[makeQuery(id+"F2.imprint","IMPRINT",EDGE,{"derivedFrom":sQuery(id+"F2.wireOp",EDGE,"E24.bottom")}),1.0]])]});
            var Q1;
            Q1=makeQuery(id+"F2.imprint","IMPRINT",FACE,{"disambiguationData":[TD([[makeQuery(id+"F2.imprint","IMPRINT",EDGE,{"derivedFrom":sQuery(id+"F2.wireOp",EDGE,"E22.bottom")}),1.0]])]});
            var Q2;
            Q2=makeQuery(id+"F2.imprint","IMPRINT",FACE,{"disambiguationData":[TD([[makeQuery(id+"F2.imprint","IMPRINT",EDGE,{"derivedFrom":sQuery(id+"F2.wireOp",EDGE,"E34.top")}),1.0]])]});
            var Q3;
            Q3=makeQuery(id+"F2.imprint","IMPRINT",FACE,{"disambiguationData":[TD([[makeQuery(id+"F2.imprint","IMPRINT",EDGE,{"derivedFrom":sQuery(id+"F2.wireOp",EDGE,"E27.bottom")}),1.0]])]});
            var Q4;
            {var subQ11=sQuery(id+"F2.wireOp",EDGE,"E52.right");Q4=makeQuery(id+"F2.imprint","IMPRINT",FACE,{"disambiguationData":[TD([[makeQuery(id+"F2.imprint","IMPRINT",EDGE,{"derivedFrom":subQ11}),-1.0]])]});}
            var Q5;
            {var subQ2=sQuery(id+"F2.wireOp",EDGE,"E60.bottom");Q5=makeQuery(id+"F2.imprint","IMPRINT",FACE,{"disambiguationData":[TD([[makeQuery(id+"F2.imprint","IMPRINT",EDGE,{"derivedFrom":subQ2}),-1.0]])]});}
            var Q6;
            Q6=makeQuery(id+"F2.imprint","IMPRINT",FACE,{"disambiguationData":[TD([[makeQuery(id+"F2.imprint","IMPRINT",EDGE,{"derivedFrom":sQuery(id+"F2.wireOp",EDGE,"E41.top")}),-1.0]])]});
            var Q7;
            Q7=makeQuery(id+"F2.imprint","IMPRINT",FACE,{"disambiguationData":[TD([[makeQuery(id+"F2.imprint","IMPRINT",EDGE,{"derivedFrom":sQuery(id+"F2.wireOp",EDGE,"E1.bottom")}),-1.0]])]});
            var Q8;
            Q8=makeQuery(id+"F2.imprint","IMPRINT",FACE,{"disambiguationData":[TD([[makeQuery(id+"F2.imprint","IMPRINT",EDGE,{"derivedFrom":sQuery(id+"F2.wireOp",EDGE,"E4.top")}),-1.0]])]});
            var Q9;
            Q9=makeQuery(id+"F2.imprint","IMPRINT",FACE,{"disambiguationData":[TD([[makeQuery(id+"F2.imprint","IMPRINT",EDGE,{"derivedFrom":sQuery(id+"F2.wireOp",EDGE,"E9.top")}),-1.0]])]});
            var Q10;
            Q10=makeQuery(id+"F2.imprint","IMPRINT",FACE,{"disambiguationData":[TD([[makeQuery(id+"F2.imprint","IMPRINT",EDGE,{"derivedFrom":sQuery(id+"F2.wireOp",EDGE,"E66.top")}),1.0]])]});
            extrude(context, id + "F5", {"entities" : qUnion([Q0, Q1, Q2, Q3, Q4, Q5, Q6, Q7, Q8, Q9, Q10]), "depth" : 203.2 * mm});
        }
        {
            var Q0;
            Q0=makeQuery(id+"F2.imprint","IMPRINT",FACE,{"disambiguationData":[TD([[makeQuery(id+"F2.imprint","IMPRINT",EDGE,{"derivedFrom":sQuery(id+"F2.wireOp",EDGE,"E22.top")}),1.0]])]});
            var Q1;
            Q1=makeQuery(id+"F2.imprint","IMPRINT",FACE,{"disambiguationData":[TD([[makeQuery(id+"F2.imprint","IMPRINT",EDGE,{"derivedFrom":sQuery(id+"F2.wireOp",EDGE,"E24.top")}),1.0]])]});
            var Q2;
            Q2=makeQuery(id+"F2.imprint","IMPRINT",FACE,{"disambiguationData":[TD([[makeQuery(id+"F2.imprint","IMPRINT",EDGE,{"derivedFrom":sQuery(id+"F2.wireOp",EDGE,"E7.top")}),-1.0]])]});
            var Q3;
            Q3=makeQuery(id+"F2.imprint","IMPRINT",FACE,{"disambiguationData":[TD([[makeQuery(id+"F2.imprint","IMPRINT",EDGE,{"derivedFrom":sQuery(id+"F2.wireOp",EDGE,"E5.top")}),-1.0]])]});
            var Q4;
            Q4=makeQuery(id+"F2.imprint","IMPRINT",FACE,{"disambiguationData":[TD([[makeQuery(id+"F2.imprint","IMPRINT",EDGE,{"derivedFrom":sQuery(id+"F2.wireOp",EDGE,"E68.bottom")}),-1.0]])]});
            var Q5;
            Q5=makeQuery(id+"F2.imprint","IMPRINT",FACE,{"disambiguationData":[TD([[makeQuery(id+"F2.imprint","IMPRINT",EDGE,{"derivedFrom":sQuery(id+"F2.wireOp",EDGE,"E79.top")}),1.0]])]});
            var Q6;
            Q6=makeQuery(id+"F2.imprint","IMPRINT",FACE,{"disambiguationData":[TD([[makeQuery(id+"F2.imprint","IMPRINT",EDGE,{"derivedFrom":sQuery(id+"F2.wireOp",EDGE,"E43.top")}),-1.0]])]});
            var Q7;
            Q7=makeQuery(id+"F2.imprint","IMPRINT",FACE,{"disambiguationData":[TD([[makeQuery(id+"F2.imprint","IMPRINT",EDGE,{"derivedFrom":sQuery(id+"F2.wireOp",EDGE,"E46.top")}),-1.0]])]});
            var Q8;
            Q8=makeQuery(id+"F2.imprint","IMPRINT",FACE,{"disambiguationData":[TD([[makeQuery(id+"F2.imprint","IMPRINT",EDGE,{"derivedFrom":sQuery(id+"F2.wireOp",EDGE,"E2.top")}),-1.0]])]});
            var Q9;
            Q9=makeQuery(id+"F2.imprint","IMPRINT",FACE,{"disambiguationData":[TD([[makeQuery(id+"F2.imprint","IMPRINT",EDGE,{"derivedFrom":sQuery(id+"F2.wireOp",EDGE,"E64.bottom")}),1.0]])]});
            var Q10;
            Q10=makeQuery(id+"F2.imprint","IMPRINT",FACE,{"disambiguationData":[TD([[makeQuery(id+"F2.imprint","IMPRINT",EDGE,{"derivedFrom":sQuery(id+"F2.wireOp",EDGE,"E81.bottom")}),-1.0]])]});
            var Q11;
            Q11=makeQuery(id+"F2.imprint","IMPRINT",FACE,{"disambiguationData":[TD([[makeQuery(id+"F2.imprint","IMPRINT",EDGE,{"derivedFrom":sQuery(id+"F2.wireOp",EDGE,"E45.top")}),-1.0]])]});
            var Q12;
            {var subQ5=sQuery(id+"F2.wireOp",EDGE,"E48.bottom");Q12=makeQuery(id+"F2.imprint","IMPRINT",FACE,{"disambiguationData":[TD([[makeQuery(id+"F2.imprint","IMPRINT",EDGE,{"derivedFrom":subQ5}),-1.0]])]});}
            var Q13;
            Q13=makeQuery(id+"F2.imprint","IMPRINT",FACE,{"disambiguationData":[TD([[makeQuery(id+"F2.imprint","IMPRINT",EDGE,{"derivedFrom":sQuery(id+"F2.wireOp",EDGE,"E40.top")}),-1.0]])]});
            extrude(context, id + "F6", {"entities" : qUnion([Q0, Q1, Q2, Q3, Q4, Q5, Q6, Q7, Q8, Q9, Q10, Q11, Q12, Q13]), "depth" : 152.4 * mm});
        }
        {
            var Q0;
            Q0=makeQuery(id+"F2.imprint","IMPRINT",FACE,{"disambiguationData":[TD([[makeQuery(id+"F2.imprint","IMPRINT",EDGE,{"derivedFrom":sQuery(id+"F2.wireOp",EDGE,"E1.top")}),-1.0]])]});
            var Q1;
            Q1=makeQuery(id+"F2.imprint","IMPRINT",FACE,{"disambiguationData":[TD([[makeQuery(id+"F2.imprint","IMPRINT",EDGE,{"derivedFrom":sQuery(id+"F2.wireOp",EDGE,"E35.top")}),1.0]])]});
            var Q2;
            Q2=makeQuery(id+"F2.imprint","IMPRINT",FACE,{"disambiguationData":[TD([[makeQuery(id+"F2.imprint","IMPRINT",EDGE,{"derivedFrom":sQuery(id+"F2.wireOp",EDGE,"E39.top")}),-1.0]])]});
            var Q3;
            Q3=makeQuery(id+"F2.imprint","IMPRINT",FACE,{"disambiguationData":[TD([[makeQuery(id+"F2.imprint","IMPRINT",EDGE,{"derivedFrom":sQuery(id+"F2.wireOp",EDGE,"E51.bottom")}),1.0]])]});
            var Q4;
            {var subQ5=sQuery(id+"F2.wireOp",EDGE,"E63.top");Q4=makeQuery(id+"F2.imprint","IMPRINT",FACE,{"disambiguationData":[TD([[makeQuery(id+"F2.imprint","IMPRINT",EDGE,{"derivedFrom":subQ5}),1.0]])]});}
            var Q5;
            Q5=makeQuery(id+"F2.imprint","IMPRINT",FACE,{"disambiguationData":[TD([[makeQuery(id+"F2.imprint","IMPRINT",EDGE,{"derivedFrom":sQuery(id+"F2.wireOp",EDGE,"E70.bottom")}),-1.0]])]});
            var Q6;
            Q6=makeQuery(id+"F2.imprint","IMPRINT",FACE,{"disambiguationData":[TD([[makeQuery(id+"F2.imprint","IMPRINT",EDGE,{"derivedFrom":sQuery(id+"F2.wireOp",EDGE,"E9.bottom")}),-1.0]])]});
            var Q7;
            {var subQ5=sQuery(id+"F2.wireOp",EDGE,"E67.bottom");Q7=makeQuery(id+"F2.imprint","IMPRINT",FACE,{"disambiguationData":[TD([[makeQuery(id+"F2.imprint","IMPRINT",EDGE,{"derivedFrom":subQ5}),1.0]])]});}
            var Q8;
            Q8=makeQuery(id+"F2.imprint","IMPRINT",FACE,{"disambiguationData":[TD([[makeQuery(id+"F2.imprint","IMPRINT",EDGE,{"derivedFrom":sQuery(id+"F2.wireOp",EDGE,"E40.bottom")}),-1.0]])]});
            extrude(context, id + "F7", {"entities" : qUnion([Q0, Q1, Q2, Q3, Q4, Q5, Q6, Q7, Q8]), "depth" : 127 * mm});
        }
        {
            var Q0;
            Q0=makeQuery(id+"F2.imprint","IMPRINT",FACE,{"disambiguationData":[TD([[makeQuery(id+"F2.imprint","IMPRINT",EDGE,{"derivedFrom":sQuery(id+"F2.wireOp",EDGE,"E8.bottom")}),-1.0]])]});
            var Q1;
            Q1=makeQuery(id+"F2.imprint","IMPRINT",FACE,{"disambiguationData":[TD([[makeQuery(id+"F2.imprint","IMPRINT",EDGE,{"derivedFrom":sQuery(id+"F2.wireOp",EDGE,"E6.bottom")}),-1.0]])]});
            var Q2;
            Q2=makeQuery(id+"F2.imprint","IMPRINT",FACE,{"disambiguationData":[TD([[makeQuery(id+"F2.imprint","IMPRINT",EDGE,{"derivedFrom":sQuery(id+"F2.wireOp",EDGE,"E3.top")}),-1.0]])]});
            var Q3;
            Q3=makeQuery(id+"F2.imprint","IMPRINT",FACE,{"disambiguationData":[TD([[makeQuery(id+"F2.imprint","IMPRINT",EDGE,{"derivedFrom":sQuery(id+"F2.wireOp",EDGE,"E20.top")}),1.0]])]});
            var Q4;
            Q4=makeQuery(id+"F2.imprint","IMPRINT",FACE,{"disambiguationData":[TD([[makeQuery(id+"F2.imprint","IMPRINT",EDGE,{"derivedFrom":sQuery(id+"F2.wireOp",EDGE,"E55.top")}),-1.0]])]});
            var Q5;
            Q5=makeQuery(id+"F2.imprint","IMPRINT",FACE,{"disambiguationData":[TD([[makeQuery(id+"F2.imprint","IMPRINT",EDGE,{"derivedFrom":sQuery(id+"F2.wireOp",EDGE,"E38.top")}),-1.0]])]});
            var Q6;
            Q6=makeQuery(id+"F2.imprint","IMPRINT",FACE,{"disambiguationData":[TD([[makeQuery(id+"F2.imprint","IMPRINT",EDGE,{"derivedFrom":sQuery(id+"F2.wireOp",EDGE,"E59.bottom")}),-1.0]])]});
            var Q7;
            Q7=makeQuery(id+"F2.imprint","IMPRINT",FACE,{"disambiguationData":[TD([[makeQuery(id+"F2.imprint","IMPRINT",EDGE,{"derivedFrom":sQuery(id+"F2.wireOp",EDGE,"E69.top")}),1.0]])]});
            extrude(context, id + "F8", {"entities" : qUnion([Q0, Q1, Q2, Q3, Q4, Q5, Q6, Q7]), "depth" : 304.8 * mm});
        }
    });
